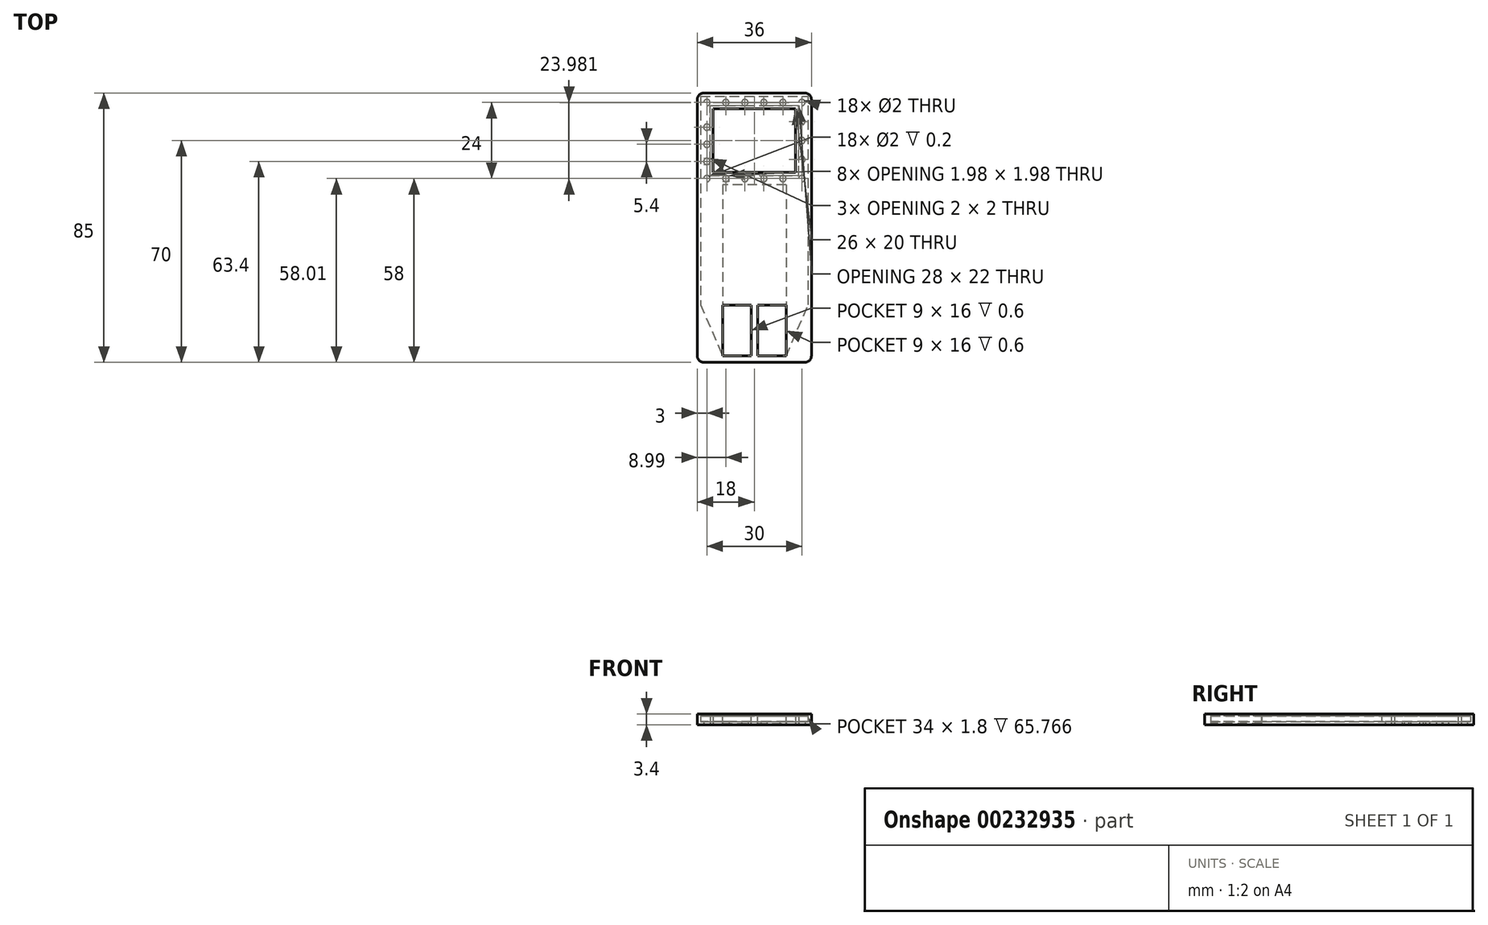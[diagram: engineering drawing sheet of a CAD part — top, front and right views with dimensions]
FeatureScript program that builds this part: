
annotation { "Feature Type Name" : "Feature", "Feature Type Description" : "" }
export const myFeature = defineFeature(function(context is Context, id is Id, definition is map)
    precondition{}
    {
        {
            var Q0;
            Q0=qCreatedBy(makeId("Top.planeOp"),FACE);
            var sketch = newSketch(context, id + "F0", { "sketchPlane" : qUnion([Q0])});
            skLineSegment(sketch, "E0.bottom", {"start": v(-13, -10) * mm, "end": v(13, -10) * mm});
            skLineSegment(sketch, "E0.top", {"start": v(-13, 10) * mm, "end": v(13, 10) * mm});
            skLineSegment(sketch, "E0.left", {"start": v(-13, -10) * mm, "end": v(-13, 10) * mm});
            skLineSegment(sketch, "E0.right", {"start": v(13, -10) * mm, "end": v(13, 10) * mm});
            skPoint(sketch, "E0.middle", {"position": v(0, 0) * mm});
            skLineSegment(sketch, "E1.0", {"start": v(-18, -15) * mm, "end": v(18, -15) * mm});
            skLineSegment(sketch, "E1.1", {"start": v(-18, -15) * mm, "end": v(-18, 15) * mm});
            skLineSegment(sketch, "E1.2", {"start": v(-18, 15) * mm, "end": v(18, 15) * mm});
            skLineSegment(sketch, "E1.3", {"start": v(18, -15) * mm, "end": v(18, 15) * mm});
            skLineSegment(sketch, "E2", {"start": v(-18, -15) * mm, "end": v(-18, -52) * mm});
            skLineSegment(sketch, "E3", {"start": v(-18, -52) * mm, "end": v(-18, -70) * mm});
            skLineSegment(sketch, "E4", {"start": v(-18, -70) * mm, "end": v(18, -70) * mm});
            skLineSegment(sketch, "E5", {"start": v(18, -70) * mm, "end": v(18, -15) * mm});
            skLineSegment(sketch, "E6", {"start": v(-18, -52) * mm, "end": v(18, -52) * mm});
            skSolve(sketch);
        }
        {
            var Q0;
            Q0 = qSketchRegion(id + "F0", true);
            extrude(context, id + "F1", {"entities" : qUnion([Q0]), "depth" : 2.4 * mm, "offsetDistance" : 25 * mm});
        }
        {
            var Q0;
            Q0=makeQuery(id+"F1.opExtrude","CAP_FACE",FACE,{"disambiguationData":[OSD([sQuery(id+"F0.wireOp",EDGE,"E0.bottom"),sQuery(id+"F0.wireOp",EDGE,"E0.top"),sQuery(id+"F0.wireOp",EDGE,"E0.left"),sQuery(id+"F0.wireOp",EDGE,"E0.right"),sQuery(id+"F0.wireOp",EDGE,"E1.1"),sQuery(id+"F0.wireOp",EDGE,"E1.2"),sQuery(id+"F0.wireOp",EDGE,"E1.3"),sQuery(id+"F0.wireOp",EDGE,"E2"),sQuery(id+"F0.wireOp",EDGE,"E3"),sQuery(id+"F0.wireOp",EDGE,"E4"),sQuery(id+"F0.wireOp",EDGE,"E5")])],"isStart":true});
            var sketch = newSketch(context, id + "F2", { "sketchPlane" : qUnion([Q0])});
            skLineSegment(sketch, "E7.0", {"start": v(-17, -14) * mm, "end": v(-17, 69) * mm});
            skLineSegment(sketch, "E7.1", {"start": v(-17, -14) * mm, "end": v(17, -14) * mm});
            skLineSegment(sketch, "E7.2", {"start": v(17, 69) * mm, "end": v(17, -14) * mm});
            skLineSegment(sketch, "E7.3", {"start": v(-17, 69) * mm, "end": v(17, 69) * mm});
            skLineSegment(sketch, "E8.0", {"start": v(14, 11) * mm, "end": v(14, -11) * mm});
            skLineSegment(sketch, "E8.1", {"start": v(-14, 11) * mm, "end": v(14, 11) * mm});
            skLineSegment(sketch, "E8.2", {"start": v(-14, 11) * mm, "end": v(-14, -11) * mm});
            skLineSegment(sketch, "E8.3", {"start": v(-14, -11) * mm, "end": v(14, -11) * mm});
            skSolve(sketch);
        }
        {
            var Q0;
            Q0=makeQuery(id+"F2.imprint","IMPRINT",FACE,{"disambiguationData":[TD([[makeQuery(id+"F2.imprint","IMPRINT",EDGE,{"derivedFrom":sQuery(id+"F2.wireOp",EDGE,"E7.0")}),-1.0]])]});
            extrude(context, id + "F3", {"entities" : qUnion([Q0]), "operationType" : NewBodyOperationType.REMOVE, "oppositeDirection" : true, "depth" : 1.8 * mm, "offsetDistance" : 25 * mm});
        }
        {
            var Q0;
            Q0=makeQuery(id+"F1.opExtrude","SWEPT_FACE",FACE,{"disambiguationData":[OSD([sQuery(id+"F0.wireOp",EDGE,"E4")])]});
            var sketch = newSketch(context, id + "F4", { "sketchPlane" : qUnion([Q0])});
            skPoint(sketch, "E9.0", {"position": v(18, 0) * mm});
            skPoint(sketch, "E10.0", {"position": v(-18, 0) * mm});
            skLineSegment(sketch, "E11", {"start": v(18, 0) * mm, "end": v(18, -1) * mm});
            skLineSegment(sketch, "E12", {"start": v(18, -1) * mm, "end": v(-18, -1) * mm});
            skLineSegment(sketch, "E13", {"start": v(-18, -1) * mm, "end": v(-18, 0) * mm});
            skSolve(sketch);
        }
        {
            var Q0;
            Q0=makeQuery(id+"F4.imprint","IMPRINT",FACE,{"disambiguationData":[TD([[makeQuery(id+"F4.imprint","IMPRINT",EDGE,{"derivedFrom":sQuery(id+"F4.wireOp",EDGE,"E11")}),-1.0]])]});
            var Q1;
            Q1=makeQuery(id+"F1.opExtrude","SWEPT_FACE",FACE,{"disambiguationData":[OSD([sQuery(id+"F0.wireOp",EDGE,"E1.2")])]});
            var Q2;
            Q2=makeQuery(id+"F1.opExtrude","SWEPT_BODY",BODY,{"disambiguationData":[OSD([sQuery(id+"F0.wireOp",EDGE,"E0.bottom"),sQuery(id+"F0.wireOp",EDGE,"E0.top"),sQuery(id+"F0.wireOp",EDGE,"E0.left"),sQuery(id+"F0.wireOp",EDGE,"E0.right"),sQuery(id+"F0.wireOp",EDGE,"E1.1"),sQuery(id+"F0.wireOp",EDGE,"E1.2"),sQuery(id+"F0.wireOp",EDGE,"E1.3"),sQuery(id+"F0.wireOp",EDGE,"E2"),sQuery(id+"F0.wireOp",EDGE,"E3"),sQuery(id+"F0.wireOp",EDGE,"E4"),sQuery(id+"F0.wireOp",EDGE,"E5")])]});
            extrude(context, id + "F5", {"entities" : qUnion([Q0]), "endBound" : BoundingType.UP_TO_SURFACE, "oppositeDirection" : true, "depth" : 25 * mm, "endBoundEntityFace" : qUnion([Q1]), "endBoundEntityBody" : qUnion([Q2]), "offsetDistance" : 25 * mm});
        }
        {
            var Q0;
            Q0=makeQuery(id+"F5.opExtrude","SWEPT_FACE",FACE,{"disambiguationData":[OSD([sQuery(id+"F4.wireOp",EDGE,"E12")])]});
            var sketch = newSketch(context, id + "F6", { "sketchPlane" : qUnion([Q0])});
            skPoint(sketch, "E14.middle", {"position": v(0, -10) * mm});
            skCircle(sketch, "E15", {"center": v(-15, -12) * mm, "radius": 1 * mm});
            skLineSegment(sketch, "E16.bottom", {"start": v(-13, 10) * mm, "end": v(13, 10) * mm});
            skLineSegment(sketch, "E16.top", {"start": v(-13, -10) * mm, "end": v(13, -10) * mm});
            skLineSegment(sketch, "E16.left", {"start": v(-13, 10) * mm, "end": v(-13, -10) * mm});
            skLineSegment(sketch, "E16.right", {"start": v(13, 10) * mm, "end": v(13, -10) * mm});
            skPoint(sketch, "E16.middle", {"position": v(0, 0) * mm});
            skCircle(sketch, "E17.1.0.0", {"center": v(-9, -12) * mm, "radius": 1 * mm});
            skCircle(sketch, "E17.2.0.0", {"center": v(-3, -12) * mm, "radius": 1 * mm});
            skCircle(sketch, "E17.3.0.0", {"center": v(3, -12) * mm, "radius": 1 * mm});
            skCircle(sketch, "E17.4.0.0", {"center": v(9, -12) * mm, "radius": 1 * mm});
            skCircle(sketch, "E17.5.0.0", {"center": v(15, -12) * mm, "radius": 1 * mm});
            skLineSegment(sketch, "E17.direction1", {"start": v(-15, -12) * mm, "end": v(-9, -12) * mm, "construction": true});
            skCircle(sketch, "E18.0.1.0", {"center": v(15, -6) * mm, "radius": 1 * mm});
            skCircle(sketch, "E18.0.2.0", {"center": v(15, 0) * mm, "radius": 1 * mm});
            skCircle(sketch, "E18.0.3.0", {"center": v(15, 6) * mm, "radius": 1 * mm});
            skCircle(sketch, "E18.0.4.0", {"center": v(15, 12) * mm, "radius": 1 * mm});
            skLineSegment(sketch, "E18.direction1", {"start": v(15, -12) * mm, "end": v(36.25, -12) * mm, "construction": true});
            skLineSegment(sketch, "E18.direction2", {"start": v(15, -12) * mm, "end": v(15, -6) * mm, "construction": true});
            skCircle(sketch, "E19.1.0.0", {"center": v(9, 12) * mm, "radius": 1 * mm});
            skCircle(sketch, "E19.2.0.0", {"center": v(3, 12) * mm, "radius": 1 * mm});
            skCircle(sketch, "E19.3.0.0", {"center": v(-3, 12) * mm, "radius": 1 * mm});
            skCircle(sketch, "E19.4.0.0", {"center": v(-9, 12) * mm, "radius": 1 * mm});
            skCircle(sketch, "E19.5.0.0", {"center": v(-15, 12) * mm, "radius": 1 * mm});
            skLineSegment(sketch, "E19.direction1", {"start": v(15, 12) * mm, "end": v(9, 12) * mm, "construction": true});
            skCircle(sketch, "E20.0.1.0", {"center": v(-15, 6.6) * mm, "radius": 1 * mm});
            skCircle(sketch, "E20.0.2.0", {"center": v(-15, 1.2) * mm, "radius": 1 * mm});
            skCircle(sketch, "E20.0.3.0", {"center": v(-15, -4.2) * mm, "radius": 1 * mm});
            skLineSegment(sketch, "E20.direction1", {"start": v(-15, 12) * mm, "end": v(13.75, 12) * mm, "construction": true});
            skLineSegment(sketch, "E20.direction2", {"start": v(-15, 12) * mm, "end": v(-15, 6.6) * mm, "construction": true});
            skSolve(sketch);
        }
        {
            var Q0;
            Q0=makeQuery(id+"F3.boolean.opBoolean","COPY",FACE,{"derivedFrom":makeQuery(id+"F3.opExtrude","CAP_FACE",FACE,{"disambiguationData":[OSD([sQuery(id+"F2.wireOp",EDGE,"E7.0"),sQuery(id+"F2.wireOp",EDGE,"E7.1"),sQuery(id+"F2.wireOp",EDGE,"E7.2"),sQuery(id+"F2.wireOp",EDGE,"E7.3"),sQuery(id+"F2.wireOp",EDGE,"E8.0"),sQuery(id+"F2.wireOp",EDGE,"E8.1"),sQuery(id+"F2.wireOp",EDGE,"E8.2"),sQuery(id+"F2.wireOp",EDGE,"E8.3")])],"isStart":false})});
            var sketch = newSketch(context, id + "F7", { "sketchPlane" : qUnion([Q0])});
            skLineSegment(sketch, "E21", {"start": v(0, 14) * mm, "end": v(-10, 14) * mm});
            skPoint(sketch, "E21.startSnap0", {"position": v(0, 11) * mm});
            skLineSegment(sketch, "E22", {"start": v(0, 14) * mm, "end": v(0, 21.87) * mm, "construction": true});
            skLineSegment(sketch, "E23", {"start": v(-10, 14) * mm, "end": v(-10, 52) * mm});
            skLineSegment(sketch, "E24", {"start": v(-10, 52) * mm, "end": v(0, 52) * mm});
            skLineSegment(sketch, "E25.MirrorCS", {"start": v(0, 14) * mm, "end": v(10, 14) * mm});
            skLineSegment(sketch, "E26.MirrorCS", {"start": v(10, 14) * mm, "end": v(10, 52) * mm});
            skLineSegment(sketch, "E27.MirrorCS", {"start": v(10, 52) * mm, "end": v(0, 52) * mm});
            skLineSegment(sketch, "E28", {"start": v(-17, 51.78) * mm, "end": v(-17, 69) * mm});
            skLineSegment(sketch, "E29", {"start": v(-17, 69) * mm, "end": v(17, 69) * mm});
            skLineSegment(sketch, "E30", {"start": v(17, 69) * mm, "end": v(17, 51.77) * mm});
            skLineSegment(sketch, "E31", {"start": v(-17, 53.81) * mm, "end": v(-17, 51.78) * mm});
            skLineSegment(sketch, "E32", {"start": v(-17, 51.78) * mm, "end": v(-10, 68.01) * mm});
            skLineSegment(sketch, "E33", {"start": v(-10, 68.01) * mm, "end": v(10, 68.01) * mm});
            skLineSegment(sketch, "E34", {"start": v(10, 68.01) * mm, "end": v(17, 51.77) * mm});
            skLineSegment(sketch, "E35", {"start": v(17, 69) * mm, "end": v(-17, 69) * mm});
            skLineSegment(sketch, "E36", {"start": v(1, 52) * mm, "end": v(1, 68.01) * mm});
            skLineSegment(sketch, "E37", {"start": v(0, 52) * mm, "end": v(0, 53.33) * mm, "construction": true});
            skLineSegment(sketch, "E38.MirrorCS", {"start": v(-1, 52) * mm, "end": v(-1, 68.01) * mm});
            skSolve(sketch);
        }
        {
            var Q0;
            Q0 = qSketchRegion(id + "F7", true);
            var Q1;
            {var subQ0=sQuery(id+"F0.wireOp",EDGE,"E0.left");var subQ1=sQuery(id+"F0.wireOp",EDGE,"E0.top");var subQ2=sQuery(id+"F0.wireOp",EDGE,"E0.right");var subQ3=sQuery(id+"F0.wireOp",EDGE,"E0.bottom");Q1=makeQuery(id+"F3.boolean.opBoolean","SPLIT",FACE,{"disambiguationData":[TD([makeQuery(id+"F1.opExtrude","SWEPT_FACE",FACE,{"disambiguationData":[OSD([subQ3])]})])],"derivedFrom":makeQuery(id+"F1.opExtrude","CAP_FACE",FACE,{"disambiguationData":[OSD([subQ3,subQ1,subQ0,subQ2,sQuery(id+"F0.wireOp",EDGE,"E1.1"),sQuery(id+"F0.wireOp",EDGE,"E1.2"),sQuery(id+"F0.wireOp",EDGE,"E1.3"),sQuery(id+"F0.wireOp",EDGE,"E2"),sQuery(id+"F0.wireOp",EDGE,"E3"),sQuery(id+"F0.wireOp",EDGE,"E4"),sQuery(id+"F0.wireOp",EDGE,"E5")])],"isStart":true})});}
            extrude(context, id + "F8", {"entities" : qUnion([Q0]), "operationType" : NewBodyOperationType.ADD, "endBound" : BoundingType.UP_TO_SURFACE, "depth" : 25 * mm, "endBoundEntityFace" : qUnion([Q1]), "offsetDistance" : 25 * mm});
        }
        {
            var Q0;
            Q0=makeQuery(id+"F6.imprint","IMPRINT",FACE,{"disambiguationData":[TD([[makeQuery(id+"F6.imprint","IMPRINT",EDGE,{"derivedFrom":sQuery(id+"F6.wireOp",EDGE,"E15")}),1.0]])]});
            var Q1;
            Q1=makeQuery(id+"F6.imprint","IMPRINT",FACE,{"disambiguationData":[TD([[makeQuery(id+"F6.imprint","IMPRINT",EDGE,{"derivedFrom":sQuery(id+"F6.wireOp",EDGE,"E17.1.0.0")}),1.0]])]});
            var Q2;
            Q2=makeQuery(id+"F6.imprint","IMPRINT",FACE,{"disambiguationData":[TD([[makeQuery(id+"F6.imprint","IMPRINT",EDGE,{"derivedFrom":sQuery(id+"F6.wireOp",EDGE,"E17.2.0.0")}),1.0]])]});
            var Q3;
            Q3=makeQuery(id+"F6.imprint","IMPRINT",FACE,{"disambiguationData":[TD([[makeQuery(id+"F6.imprint","IMPRINT",EDGE,{"derivedFrom":sQuery(id+"F6.wireOp",EDGE,"E17.3.0.0")}),1.0]])]});
            var Q4;
            Q4=makeQuery(id+"F6.imprint","IMPRINT",FACE,{"disambiguationData":[TD([[makeQuery(id+"F6.imprint","IMPRINT",EDGE,{"derivedFrom":sQuery(id+"F6.wireOp",EDGE,"E17.4.0.0")}),1.0]])]});
            var Q5;
            Q5=makeQuery(id+"F6.imprint","IMPRINT",FACE,{"disambiguationData":[TD([[makeQuery(id+"F6.imprint","IMPRINT",EDGE,{"derivedFrom":sQuery(id+"F6.wireOp",EDGE,"E17.5.0.0")}),1.0]])]});
            var Q6;
            Q6=makeQuery(id+"F6.imprint","IMPRINT",FACE,{"disambiguationData":[TD([[makeQuery(id+"F6.imprint","IMPRINT",EDGE,{"derivedFrom":sQuery(id+"F6.wireOp",EDGE,"E18.0.1.0")}),1.0]])]});
            var Q7;
            Q7=makeQuery(id+"F6.imprint","IMPRINT",FACE,{"disambiguationData":[TD([[makeQuery(id+"F6.imprint","IMPRINT",EDGE,{"derivedFrom":sQuery(id+"F6.wireOp",EDGE,"E18.0.2.0")}),1.0]])]});
            var Q8;
            Q8=makeQuery(id+"F6.imprint","IMPRINT",FACE,{"disambiguationData":[TD([[makeQuery(id+"F6.imprint","IMPRINT",EDGE,{"derivedFrom":sQuery(id+"F6.wireOp",EDGE,"E18.0.3.0")}),1.0]])]});
            var Q9;
            Q9=makeQuery(id+"F6.imprint","IMPRINT",FACE,{"disambiguationData":[TD([[makeQuery(id+"F6.imprint","IMPRINT",EDGE,{"derivedFrom":sQuery(id+"F6.wireOp",EDGE,"E18.0.4.0")}),1.0]])]});
            var Q10;
            Q10=makeQuery(id+"F6.imprint","IMPRINT",FACE,{"disambiguationData":[TD([[makeQuery(id+"F6.imprint","IMPRINT",EDGE,{"derivedFrom":sQuery(id+"F6.wireOp",EDGE,"E19.1.0.0")}),1.0]])]});
            var Q11;
            Q11=makeQuery(id+"F6.imprint","IMPRINT",FACE,{"disambiguationData":[TD([[makeQuery(id+"F6.imprint","IMPRINT",EDGE,{"derivedFrom":sQuery(id+"F6.wireOp",EDGE,"E19.2.0.0")}),1.0]])]});
            var Q12;
            Q12=makeQuery(id+"F6.imprint","IMPRINT",FACE,{"disambiguationData":[TD([[makeQuery(id+"F6.imprint","IMPRINT",EDGE,{"derivedFrom":sQuery(id+"F6.wireOp",EDGE,"E19.3.0.0")}),1.0]])]});
            var Q13;
            Q13=makeQuery(id+"F6.imprint","IMPRINT",FACE,{"disambiguationData":[TD([[makeQuery(id+"F6.imprint","IMPRINT",EDGE,{"derivedFrom":sQuery(id+"F6.wireOp",EDGE,"E19.4.0.0")}),1.0]])]});
            var Q14;
            Q14=makeQuery(id+"F6.imprint","IMPRINT",FACE,{"disambiguationData":[TD([[makeQuery(id+"F6.imprint","IMPRINT",EDGE,{"derivedFrom":sQuery(id+"F6.wireOp",EDGE,"E19.5.0.0")}),1.0]])]});
            var Q15;
            Q15=makeQuery(id+"F6.imprint","IMPRINT",FACE,{"disambiguationData":[TD([[makeQuery(id+"F6.imprint","IMPRINT",EDGE,{"derivedFrom":sQuery(id+"F6.wireOp",EDGE,"E20.0.1.0")}),1.0]])]});
            var Q16;
            Q16=makeQuery(id+"F6.imprint","IMPRINT",FACE,{"disambiguationData":[TD([[makeQuery(id+"F6.imprint","IMPRINT",EDGE,{"derivedFrom":sQuery(id+"F6.wireOp",EDGE,"E20.0.2.0")}),1.0]])]});
            var Q17;
            Q17=makeQuery(id+"F6.imprint","IMPRINT",FACE,{"disambiguationData":[TD([[makeQuery(id+"F6.imprint","IMPRINT",EDGE,{"derivedFrom":sQuery(id+"F6.wireOp",EDGE,"E20.0.3.0")}),1.0]])]});
            var Q18;
            Q18=makeQuery(id+"F6.imprint","IMPRINT",FACE,{"disambiguationData":[TD([[makeQuery(id+"F6.imprint","IMPRINT",EDGE,{"derivedFrom":sQuery(id+"F6.wireOp",EDGE,"9aPwL6ad-gpLs-ygax-PKFa-AAPFtlQL0jBM.bottom")}),-1.0]])]});
            extrude(context, id + "F9", {"entities" : qUnion([Q0, Q1, Q2, Q3, Q4, Q5, Q6, Q7, Q8, Q9, Q10, Q11, Q12, Q13, Q14, Q15, Q16, Q17, Q18]), "operationType" : NewBodyOperationType.REMOVE, "oppositeDirection" : true, "depth" : 3 * mm, "offsetDistance" : 25 * mm});
        }
        {
            var Q0;
            Q0=makeQuery(id+"F1.opExtrude","CAP_FACE",FACE,{"disambiguationData":[OSD([sQuery(id+"F0.wireOp",EDGE,"E0.bottom"),sQuery(id+"F0.wireOp",EDGE,"E0.top"),sQuery(id+"F0.wireOp",EDGE,"E0.left"),sQuery(id+"F0.wireOp",EDGE,"E0.right"),sQuery(id+"F0.wireOp",EDGE,"E1.1"),sQuery(id+"F0.wireOp",EDGE,"E1.2"),sQuery(id+"F0.wireOp",EDGE,"E1.3"),sQuery(id+"F0.wireOp",EDGE,"E2"),sQuery(id+"F0.wireOp",EDGE,"E3"),sQuery(id+"F0.wireOp",EDGE,"E4"),sQuery(id+"F0.wireOp",EDGE,"E5")])],"isStart":false});
            var sketch = newSketch(context, id + "F10", { "sketchPlane" : qUnion([Q0])});
            skLineSegment(sketch, "E39.bottom", {"start": v(-10, -52) * mm, "end": v(10, -52) * mm});
            skLineSegment(sketch, "E39.top", {"start": v(-10, -68) * mm, "end": v(10, -68) * mm});
            skLineSegment(sketch, "E39.left", {"start": v(-10, -52) * mm, "end": v(-10, -68) * mm});
            skLineSegment(sketch, "E39.right", {"start": v(10, -52) * mm, "end": v(10, -68) * mm});
            skPoint(sketch, "E39.middle", {"position": v(0, -60) * mm});
            skLineSegment(sketch, "E40", {"start": v(-1, -52) * mm, "end": v(-1, -68) * mm});
            skLineSegment(sketch, "E41", {"start": v(0, -60) * mm, "end": v(0, -58.03) * mm, "construction": true});
            skLineSegment(sketch, "E42.MirrorCS", {"start": v(1, -52) * mm, "end": v(1, -68) * mm});
            skSolve(sketch);
        }
        {
            var Q0;
            Q0=makeQuery(id+"F6.imprint","IMPRINT",FACE,{"disambiguationData":[TD([[makeQuery(id+"F6.imprint","IMPRINT",EDGE,{"derivedFrom":sQuery(id+"F6.wireOp",EDGE,"E16.bottom")}),-1.0]])]});
            extrude(context, id + "F11", {"entities" : qUnion([Q0]), "operationType" : NewBodyOperationType.REMOVE, "oppositeDirection" : true, "depth" : 25 * mm, "offsetDistance" : 25 * mm});
        }
        {
            var Q0;
            Q0=makeQuery(id+"F1.opExtrude","SWEPT_EDGE",EDGE,{"disambiguationData":[OSD([sQuery(id+"F0.wireOp",EDGE,"E1.2"),sQuery(id+"F0.wireOp",EDGE,"E1.3")])]});
            var Q1;
            Q1=makeQuery(id+"F5.opExtrude","CAP_EDGE",EDGE,{"disambiguationData":[OSD([sQuery(id+"F4.wireOp",EDGE,"E11")])],"isStart":false});
            var Q2;
            Q2=makeQuery(id+"F1.opExtrude","SWEPT_EDGE",EDGE,{"disambiguationData":[OSD([sQuery(id+"F0.wireOp",EDGE,"E4"),sQuery(id+"F0.wireOp",EDGE,"E5")])]});
            var Q3;
            Q3=makeQuery(id+"F5.opExtrude","CAP_EDGE",EDGE,{"disambiguationData":[OSD([sQuery(id+"F4.wireOp",EDGE,"E11")])],"isStart":true});
            var Q4;
            Q4=makeQuery(id+"F1.opExtrude","SWEPT_EDGE",EDGE,{"disambiguationData":[OSD([sQuery(id+"F0.wireOp",EDGE,"E3"),sQuery(id+"F0.wireOp",EDGE,"E4")])]});
            var Q5;
            Q5=makeQuery(id+"F5.opExtrude","CAP_EDGE",EDGE,{"disambiguationData":[OSD([sQuery(id+"F4.wireOp",EDGE,"E13")])],"isStart":true});
            var Q6;
            Q6=makeQuery(id+"F1.opExtrude","SWEPT_EDGE",EDGE,{"disambiguationData":[OSD([sQuery(id+"F0.wireOp",EDGE,"E1.1"),sQuery(id+"F0.wireOp",EDGE,"E1.2")])]});
            var Q7;
            Q7=makeQuery(id+"F5.opExtrude","CAP_EDGE",EDGE,{"disambiguationData":[OSD([sQuery(id+"F4.wireOp",EDGE,"E13")])],"isStart":false});
            fillet(context, id + "F12", {"entities" : qUnion([Q0, Q1, Q2, Q3, Q4, Q5, Q6, Q7]), "radius" : 2 * mm, "tangentPropagation" : true, "allowEdgeOverflow" : false});
        }
        {
            var Q0;
            {var subQ0=sQuery(id+"F10.wireOp",EDGE,"E39.right");Q0=makeQuery(id+"F10.imprint","IMPRINT",FACE,{"disambiguationData":[TD([[makeQuery(id+"F10.imprint","IMPRINT",EDGE,{"derivedFrom":subQ0}),-1.0]])]});}
            var Q1;
            {var subQ0=sQuery(id+"F10.wireOp",EDGE,"E39.left");Q1=makeQuery(id+"F10.imprint","IMPRINT",FACE,{"disambiguationData":[TD([[makeQuery(id+"F10.imprint","IMPRINT",EDGE,{"derivedFrom":subQ0}),1.0]])]});}
            extrude(context, id + "F13", {"entities" : qUnion([Q0, Q1]), "operationType" : NewBodyOperationType.REMOVE, "oppositeDirection" : true, "depth" : 3 * mm, "offsetDistance" : 25 * mm});
        }
    });
